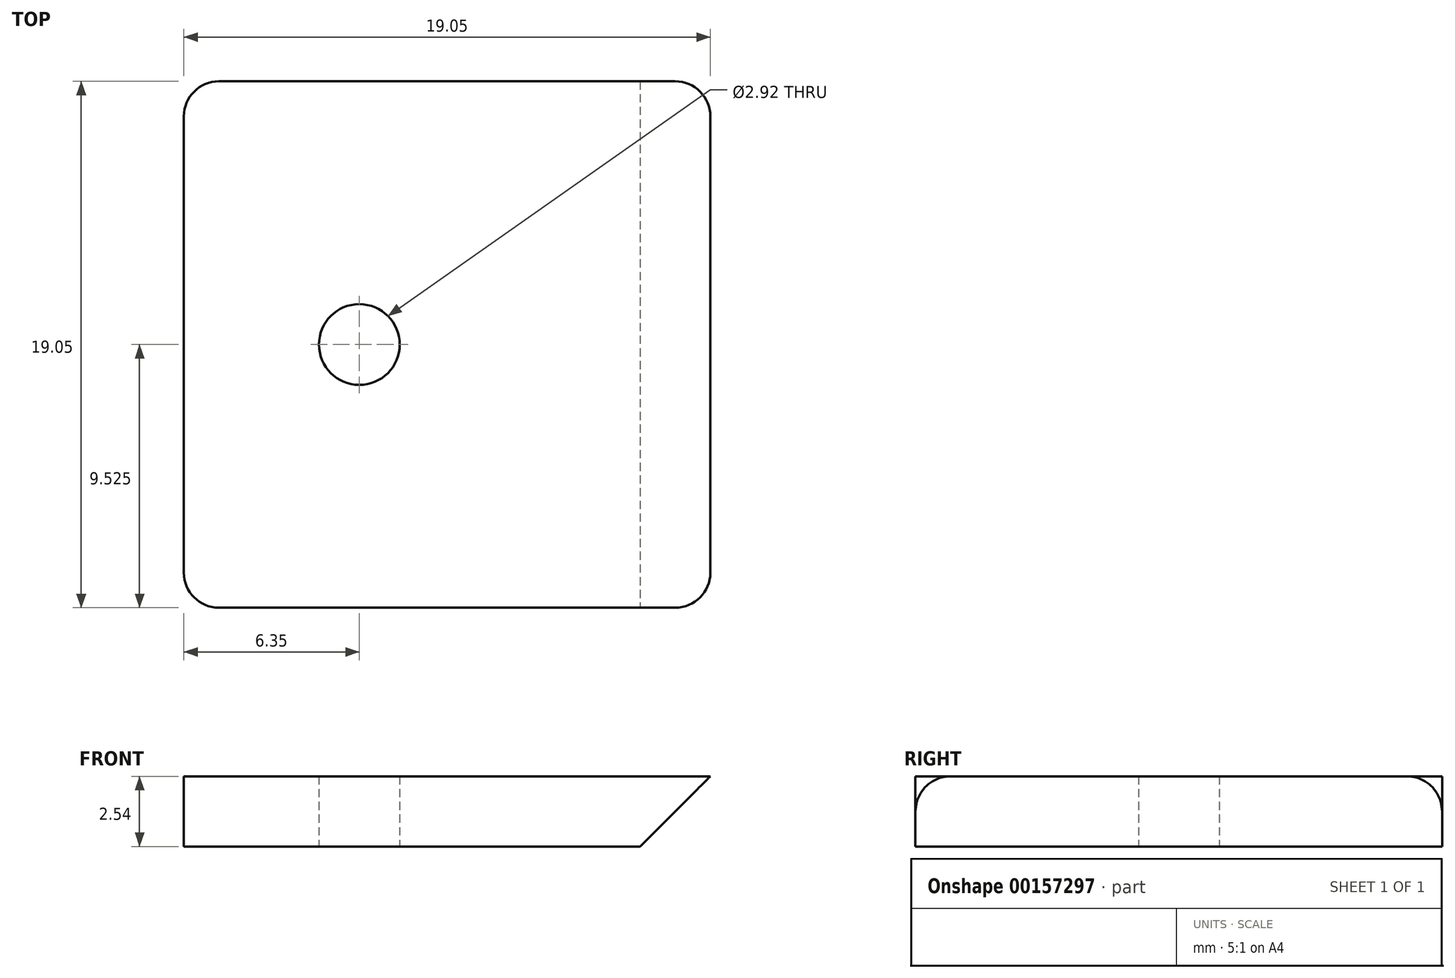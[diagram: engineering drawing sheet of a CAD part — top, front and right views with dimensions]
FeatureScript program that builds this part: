
annotation { "Feature Type Name" : "Feature", "Feature Type Description" : "" }
export const myFeature = defineFeature(function(context is Context, id is Id, definition is map)
    precondition{}
    {
        {
            var Q0;
            Q0=qCreatedBy(makeId("Top.planeOp"),FACE);
            var sketch = newSketch(context, id + "F0", { "sketchPlane" : qUnion([Q0])});
            skLineSegment(sketch, "E0.bottom", {"start": v(-3.8, 2.54) * mm, "end": v(-20.32, 2.54) * mm});
            skLineSegment(sketch, "E0.top", {"start": v(-3.81, 21.6) * mm, "end": v(-20.32, 21.59) * mm});
            skLineSegment(sketch, "E0.left", {"start": v(-2.54, 3.81) * mm, "end": v(-2.54, 20.32) * mm});
            skLineSegment(sketch, "E0.right", {"start": v(-21.59, 3.8) * mm, "end": v(-21.59, 20.32) * mm});
            skCircle(sketch, "E1", {"center": v(-15.24, 12.06) * mm, "radius": 1.46 * mm});
            skPoint(sketch, "E2.visualSharp", {"position": v(-21.59, 21.59) * mm});
            skArc(sketch, "E2.filletArc", {"start": v(-20.32, 21.59) * mm, "mid": v(-21.22, 21.22) * mm, "end": v(-21.6, 20.32) * mm});
            skPoint(sketch, "E3.visualSharp", {"position": v(-21.59, 2.54) * mm});
            skArc(sketch, "E3.filletArc", {"start": v(-21.59, 3.8) * mm, "mid": v(-21.22, 2.91) * mm, "end": v(-20.32, 2.54) * mm});
            skPoint(sketch, "E4.visualSharp", {"position": v(-2.54, 2.54) * mm});
            skArc(sketch, "E4.filletArc", {"start": v(-3.8, 2.54) * mm, "mid": v(-2.91, 2.91) * mm, "end": v(-2.54, 3.81) * mm});
            skPoint(sketch, "E5.visualSharp", {"position": v(-2.54, 21.6) * mm});
            skArc(sketch, "E5.filletArc", {"start": v(-2.54, 20.32) * mm, "mid": v(-2.91, 21.22) * mm, "end": v(-3.81, 21.6) * mm});
            skSolve(sketch);
        }
        {
            var Q0;
            Q0 = qSketchRegion(id + "F0", true);
            extrude(context, id + "F1", {"entities" : qUnion([Q0]), "depth" : 2.54 * mm});
        }
        {
            var Q0;
            Q0=makeQuery(id+"F1.opExtrude","CAP_EDGE",EDGE,{"disambiguationData":[OSD([sQuery(id+"F0.wireOp",EDGE,"aoFGCnl5-8QuO-vPEJ-kxt0-NOLUgm0tsGH0.right")])],"isStart":true});
            var Q1;
            Q1=makeQuery(id+"F1.opExtrude","CAP_EDGE",EDGE,{"disambiguationData":[OSD([sQuery(id+"F0.wireOp",EDGE,"E0.left")])],"isStart":true});
            var Q2;
            Q2=makeQuery(id+"F1.opExtrude","CAP_EDGE",EDGE,{"disambiguationData":[OSD([sQuery(id+"F0.wireOp",EDGE,"e25cd414-2625-4b40-bf3a-258921b512e30.MirrorCS")])],"isStart":true});
            var Q3;
            Q3=makeQuery(id+"F1.opExtrude","CAP_EDGE",EDGE,{"disambiguationData":[OSD([sQuery(id+"F0.wireOp",EDGE,"b036b5cd-ad19-4a47-85a8-a4cf124e688e0.MirrorCS")])],"isStart":true});
            var Q4;
            Q4=makeQuery(id+"F1.opExtrude","CAP_EDGE",EDGE,{"disambiguationData":[OSD([sQuery(id+"F0.wireOp",EDGE,"d25565d4-ebb5-467f-8d2a-e91fe5e9bfc70.MirrorCS")])],"isStart":true});
            var Q5;
            Q5=makeQuery(id+"F1.opExtrude","CAP_EDGE",EDGE,{"disambiguationData":[OSD([sQuery(id+"F0.wireOp",EDGE,"27786aca-3c40-438b-a6cd-37362562149c0.MirrorCS")])],"isStart":true});
            var Q6;
            Q6=makeQuery(id+"F1.opExtrude","CAP_EDGE",EDGE,{"disambiguationData":[OSD([sQuery(id+"F0.wireOp",EDGE,"7d3a53ed-7c70-4c9d-a47d-9624aae9d9ff0.MirrorCS")])],"isStart":true});
            var Q7;
            Q7=makeQuery(id+"F1.opExtrude","CAP_EDGE",EDGE,{"disambiguationData":[OSD([sQuery(id+"F0.wireOp",EDGE,"f2368ecd-0132-4f6e-97d3-aade73f3e56e0.MirrorCS")])],"isStart":true});
            chamfer(context, id + "F2", {"entities" : qUnion([Q0, Q1, Q2, Q3, Q4, Q5, Q6, Q7]), "width" : 2.54 * mm});
        }
    });
